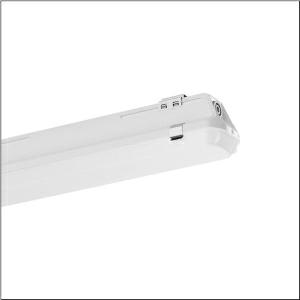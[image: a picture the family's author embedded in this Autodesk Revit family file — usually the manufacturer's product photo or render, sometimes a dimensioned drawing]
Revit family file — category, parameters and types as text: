
# Revit family: monsun_r__11_parking_51fg20dp440hhq_4cc6
name_source: partatom
category: Lighting Fixtures
units: mm (PartAtom-declared; Revit-internal decimal feet)

## family parameters
Cut with Voids When Loaded = No
Host = Face
Light Source = No
Part Type = Normal
Room Calculation Point = No
Round Connector Dimension = Use Diameter
Shared = No

## types (1)
- --- (1 x LED, 4840 lm, 31.3 W, 4000K)
    Apparent Load = 31 VA
    CIE Flux Codes = 45 75 93 94 100
    Color Rendering = 80
    Color Temperature = 4000K
    Default Elevation = 1800 mm
    Description = Monsun® 11 parking, damp-proof luminaire, chain hanger, primary optical cover: enclosure, of PC, light emission: direct distribution, primary light characteristic: symmetric, installation type: suspended mounting, surface-mounted, horizontal mounting, vertical mounting, LED, rated luminous flux: 4.840lm, luminous efficacy: 157lm/W, light colour: 840, colour temperature: 4000K, control gear: ECG DALI, with terminal, 5-pole, max. 2.5mm², mains connection: 220..240V, AC, 50/60Hz, rated input power: 31W, housing, of glass-fibre reinforced polyester, uncoated, bright grey, incl. chain hanger, length: 1.590mm, width: 90mm, height: 88mm, clip for enclosure, of stainless steel (V2A), ceiling mounting element, of stainless steel (V2A), chain hanger, of stainless steel (V2A), multi-sensor HC1, local controlcentral control, equipment: slave, scope of services: certified according to part 101,103,303,304, dimmable, protection rating (complete): IP66, insulation class (complete): insulation class I (protective earthing), certification: CE, ENEC, VDE, UKCA, protection symbol: D, impact resistance: IK08, permissible operating ambient temperature: -25..+40°C, standard: EN 50419, EN 60598-2-1, corresponds to IFS (International Featured Standards) requirements for safety and quality in the food industry, for indoor or canopied outdoor use, no direct snow, no direct sun, no direct rain, contact your sales advisor before using the luminaires in applications with unclear chemical exposure, large temperature fluctuations or condensation-forming humidity, LABS conformity tested according to VDMA 24364:2018-05, packaging unit: 1 piece
    Height = 89 mm
    Lamp = 1 x LED
    Lamp Light Flux = 4840 lm
    Lamp Power = 31.3 W
    Lamp count = 1
    Length = 1590 mm
    Luminous efficacy = 155 lm/W
    Manufacturer = Siteco
    ModVariant = No
    Model = 51FG20DP440HHQ
    Mounting Place = Ceiling
    Mounting Type = Surface mounted
    Number of Poles = 1
    OnlyDefault = Yes
    Power Factor = 1
    Product Name = Monsun® 11 parking
    Product group = damp-proof luminaire
    ProductGroupID = 301
    Protection Class = Protection class I
    Protection Degree = IP 66
    RLX_Detail_Level = 1
    RLX_Emergency_Light_Flux = 0 lm
    RLX_Emergency_Type = 0
    RLX_Emergency_Type_DB = No
    RlxData = <blob elided: 91953 chars, md5=625e4ab0>
    Socket = socket
    Standby Power = 0 W
    System Light Flux = 4840 lm
    System Power = 31 W
    Type Comments = factory setting: luminous flux: 100 % | dim-lin: 254 | 205 mA
    Type Image = l_1004748.jpg
    URL = http://relux.com
    VarID = @adj_092755
    Voltage = 0 V
    Weight = 0.00 kg
    Width = 90 mm

## geometry (parser evidence)
native form markers: Blend x4, Sweep x14
no freeform markers — native parametric forms only
